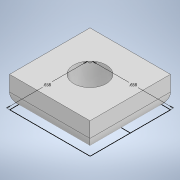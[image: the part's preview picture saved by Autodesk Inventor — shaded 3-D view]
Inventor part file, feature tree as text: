
AUTODESK INVENTOR PART (.ipt)
format: ipt  version: 2020 (Build 240168000, 168)  size: 119,808 bytes
history: native  units: in
note: dims shown in document units (in); Inventor stores cm internally (conversion verified against a paired STEP export)
features: sketch x1, extrude x1, hole x1, fillet x1
ambient origin geometry x8: Origin, YZ Plane, XZ Plane, XY Plane, X Axis, Y Axis, Z Axis, Center Point
bodies: Solid1 (feature_tree)
feature tree (4):
  sketch  "Sketch1"  dims[d0=0.658in d1=0.658in d2=0.25in d3=0.0in d4=0.266in d5=0.75in d6=0.438in d7=0.0625in d8=0.5635in d9=1.0in d10=0.8108in d11=0.125in]
  extrude  "Extrusion1"  Depth=0.125in
  hole  "Hole1"  [1 undecoded]
  fillet  "Fillet1"  Radius=0.125in
note: 1 required parameter value undecoded (feature->parameter linkage not recoverable at this tier; creation-order binding heuristic only, values carry confidence <= 0.55)
